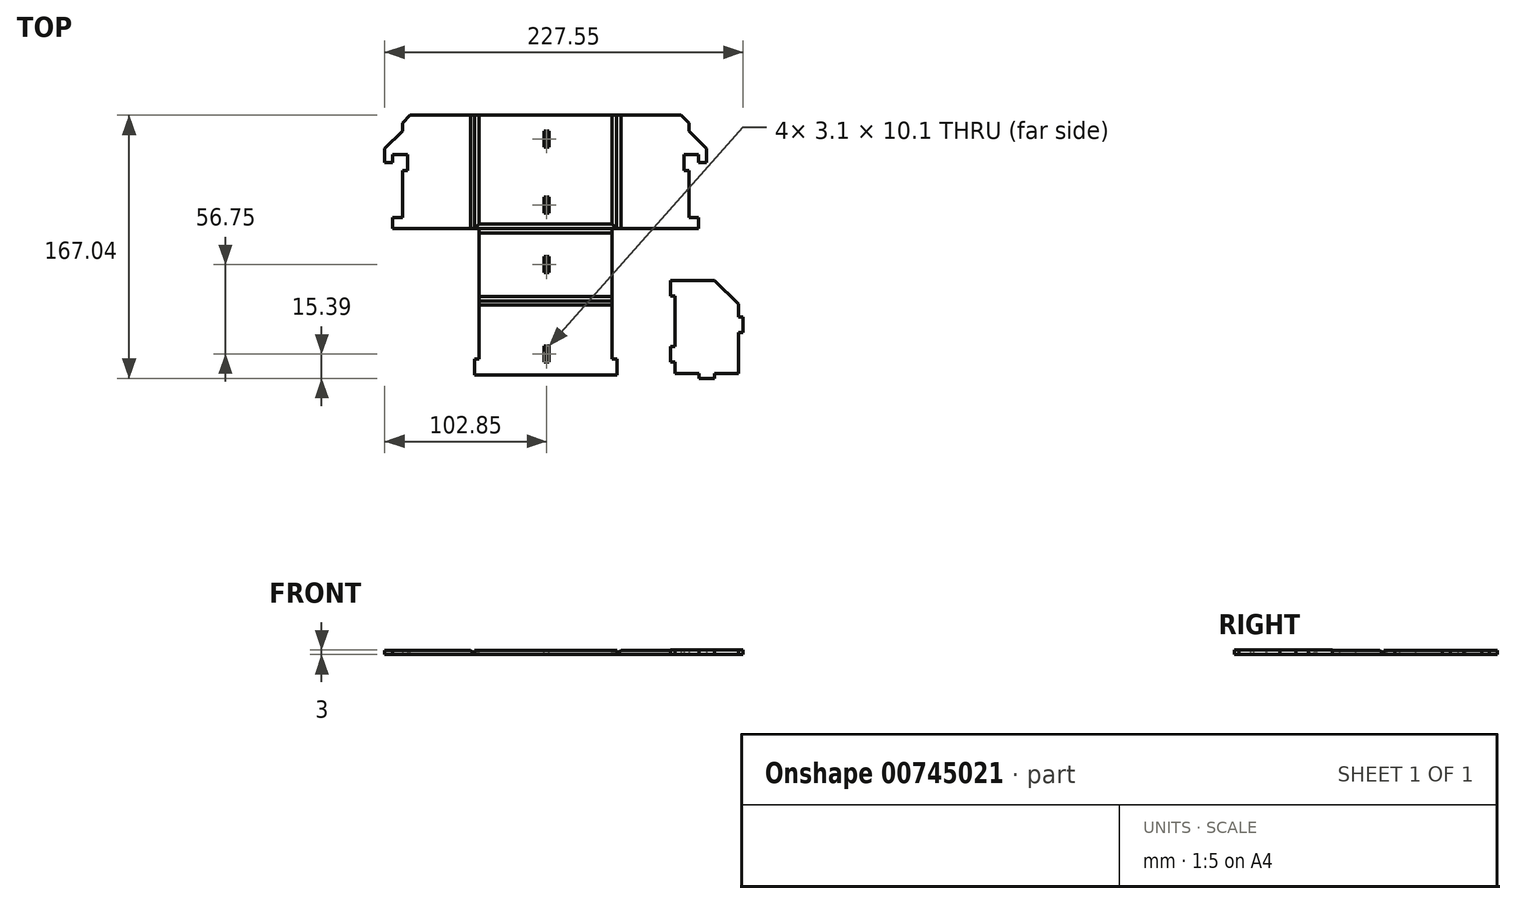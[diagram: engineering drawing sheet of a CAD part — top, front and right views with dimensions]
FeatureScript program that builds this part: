
annotation { "Feature Type Name" : "Feature", "Feature Type Description" : "" }
export const myFeature = defineFeature(function(context is Context, id is Id, definition is map)
    precondition{}
    {
        {
            var Q0;
            Q0=qCreatedBy(makeId("Top.planeOp"),FACE);
            var sketch = newSketch(context, id + "F0", { "sketchPlane" : qUnion([Q0])});
            skLineSegment(sketch, "E0.bottom", {"start": v(45, -36) * mm, "end": v(-45, -36) * mm});
            skLineSegment(sketch, "E0.top", {"start": v(45, 36) * mm, "end": v(-45, 36) * mm});
            skLineSegment(sketch, "E0.left", {"start": v(45, -36) * mm, "end": v(45, 36) * mm});
            skLineSegment(sketch, "E0.right", {"start": v(-45, -36) * mm, "end": v(-45, 36) * mm});
            skPoint(sketch, "E0.middle", {"position": v(0, 0) * mm});
            skLineSegment(sketch, "E1.bottom", {"start": v(45, 36) * mm, "end": v(91, 36) * mm});
            skLineSegment(sketch, "E1.top", {"start": v(45, -36) * mm, "end": v(91, -36) * mm});
            skLineSegment(sketch, "E1.left", {"start": v(45, 36) * mm, "end": v(45, -36) * mm});
            skLineSegment(sketch, "E1.right", {"start": v(91, 1) * mm, "end": v(91, -29) * mm});
            skLineSegment(sketch, "E2.bottom", {"start": v(-45, 36) * mm, "end": v(-91, 36) * mm});
            skLineSegment(sketch, "E2.top", {"start": v(-45, -36) * mm, "end": v(-91, -36) * mm});
            skLineSegment(sketch, "E2.left", {"start": v(-45, 36) * mm, "end": v(-45, -36) * mm});
            skLineSegment(sketch, "E2.right", {"start": v(-91, 36) * mm, "end": v(-91, 26) * mm});
            skLineSegment(sketch, "E3", {"start": v(91, 11) * mm, "end": v(97.2, 11) * mm});
            skLineSegment(sketch, "E4", {"start": v(97.2, 11) * mm, "end": v(97.2, 6) * mm});
            skLineSegment(sketch, "E5", {"start": v(97.2, 6) * mm, "end": v(102.2, 6) * mm});
            skPoint(sketch, "E6", {"position": v(102.2, 6) * mm});
            skLineSegment(sketch, "E7.bottom", {"start": v(91, -36) * mm, "end": v(97.2, -36) * mm});
            skLineSegment(sketch, "E7.top", {"start": v(91, -29) * mm, "end": v(97.2, -29) * mm});
            skLineSegment(sketch, "E7.right", {"start": v(97.2, -36) * mm, "end": v(97.2, -29) * mm});
            skLineSegment(sketch, "E8", {"start": v(91, 36) * mm, "end": v(91, 26) * mm});
            skLineSegment(sketch, "E9", {"start": v(91, 26) * mm, "end": v(102.2, 14.8) * mm});
            skLineSegment(sketch, "E10", {"start": v(102.2, 6) * mm, "end": v(102.2, 14.8) * mm});
            skLineSegment(sketch, "E11.MirrorCS", {"start": v(-91, 26) * mm, "end": v(-102.2, 14.8) * mm});
            skLineSegment(sketch, "E12.MirrorCS", {"start": v(-102.2, 6) * mm, "end": v(-102.2, 14.8) * mm});
            skLineSegment(sketch, "E13.MirrorCS", {"start": v(-97.2, 6) * mm, "end": v(-102.2, 6) * mm});
            skLineSegment(sketch, "E14.MirrorCS", {"start": v(-97.2, 11) * mm, "end": v(-97.2, 6) * mm});
            skLineSegment(sketch, "E15.MirrorCS", {"start": v(-91, 11) * mm, "end": v(-97.2, 11) * mm});
            skLineSegment(sketch, "E16.MirrorCS", {"start": v(-91, -29) * mm, "end": v(-97.2, -29) * mm});
            skLineSegment(sketch, "E17.MirrorCS", {"start": v(-97.2, -36) * mm, "end": v(-97.2, -29) * mm});
            skLineSegment(sketch, "E18.MirrorCS", {"start": v(-91, -36) * mm, "end": v(-97.2, -36) * mm});
            skLineSegment(sketch, "E19.trimOffspring", {"start": v(-91, 1) * mm, "end": v(-91, -29) * mm});
            skLineSegment(sketch, "E20.bottom", {"start": v(-42.2, -36) * mm, "end": v(42.2, -36) * mm});
            skLineSegment(sketch, "E20.top", {"start": v(-42.2, -81.8) * mm, "end": v(42.2, -81.8) * mm});
            skLineSegment(sketch, "E20.left", {"start": v(-42.2, -36) * mm, "end": v(-42.2, -81.8) * mm});
            skLineSegment(sketch, "E20.right", {"start": v(42.2, -36) * mm, "end": v(42.2, -81.8) * mm});
            skLineSegment(sketch, "E21.top", {"start": v(-42.2, -128.8) * mm, "end": v(42.2, -128.8) * mm});
            skLineSegment(sketch, "E21.left", {"start": v(-42.2, -81.8) * mm, "end": v(-42.2, -128.8) * mm});
            skLineSegment(sketch, "E21.right", {"start": v(42.2, -81.8) * mm, "end": v(42.2, -128.8) * mm});
            skLineSegment(sketch, "E22", {"start": v(91, 11) * mm, "end": v(87.8, 11) * mm});
            skLineSegment(sketch, "E23", {"start": v(87.8, 11) * mm, "end": v(87.8, 1) * mm});
            skLineSegment(sketch, "E24", {"start": v(87.8, 1) * mm, "end": v(91, 1) * mm});
            skLineSegment(sketch, "E25.MirrorCS", {"start": v(-91, 11) * mm, "end": v(-87.8, 11) * mm});
            skLineSegment(sketch, "E26.MirrorCS", {"start": v(-87.8, 11) * mm, "end": v(-87.8, 1) * mm});
            skLineSegment(sketch, "E27.MirrorCS", {"start": v(-87.8, 1) * mm, "end": v(-91, 1) * mm});
            skSolve(sketch);
        }
        {
            var Q0;
            Q0=makeQuery(id+"F0.imprint","IMPRINT",FACE,{"disambiguationData":[TD([[makeQuery(id+"F0.imprint","IMPRINT",EDGE,{"derivedFrom":sQuery(id+"F0.wireOp",EDGE,"E0.right")}),1.0]])]});
            var Q1;
            Q1=makeQuery(id+"F0.imprint","IMPRINT",FACE,{"disambiguationData":[TD([[makeQuery(id+"F0.imprint","IMPRINT",EDGE,{"derivedFrom":sQuery(id+"F0.wireOp",EDGE,"E0.left")}),-1.0]])]});
            extrude(context, id + "F1", {"entities" : qUnion([Q0, Q1]), "depth" : 2.8 * mm, "offsetDistance" : 25 * mm});
        }
        {
            var Q0;
            Q0=makeQuery(id+"F1.opExtrude","CAP_EDGE",EDGE,{"disambiguationData":[OSD([sQuery(id+"F0.wireOp",EDGE,"E0.left")])],"isStart":false});
            var Q1;
            Q1=makeQuery(id+"F1.opExtrude","CAP_EDGE",EDGE,{"disambiguationData":[OSD([sQuery(id+"F0.wireOp",EDGE,"E0.right")])],"isStart":false});
            chamfer(context, id + "F2", {"entities" : qUnion([Q0, Q1]), "width" : 2.8 * mm, "tangentPropagation" : true});
        }
        {
            var Q0;
            Q0=makeQuery(id+"F0.imprint","IMPRINT",FACE,{"disambiguationData":[TD([[makeQuery(id+"F0.imprint","IMPRINT",EDGE,{"derivedFrom":sQuery(id+"F0.wireOp",EDGE,"E0.top")}),1.0]])]});
            extrude(context, id + "F3", {"entities" : qUnion([Q0]), "depth" : 2.8 * mm, "offsetDistance" : 25 * mm});
        }
        {
            var Q0;
            Q0=makeQuery(id+"F3.opExtrude","CAP_EDGE",EDGE,{"disambiguationData":[OSD([sQuery(id+"F0.wireOp",EDGE,"E0.left")])],"isStart":false});
            var Q1;
            Q1=makeQuery(id+"F3.opExtrude","CAP_EDGE",EDGE,{"disambiguationData":[OSD([sQuery(id+"F0.wireOp",EDGE,"E0.right")])],"isStart":false});
            var Q2;
            Q2=makeQuery(id+"F3.opExtrude","CAP_EDGE",EDGE,{"disambiguationData":[OSD([sQuery(id+"F0.wireOp",EDGE,"E0.bottom")])],"isStart":false});
            chamfer(context, id + "F4", {"entities" : qUnion([Q0, Q1, Q2]), "width" : 2.8 * mm, "tangentPropagation" : true});
        }
        {
            var Q0;
            Q0=makeQuery(id+"F3.opExtrude","CAP_FACE",FACE,{"disambiguationData":[OSD([sQuery(id+"F0.wireOp",EDGE,"E0.bottom"),sQuery(id+"F0.wireOp",EDGE,"E0.top"),sQuery(id+"F0.wireOp",EDGE,"E0.left"),sQuery(id+"F0.wireOp",EDGE,"E0.right")])],"isStart":false});
            var sketch = newSketch(context, id + "F5", { "sketchPlane" : qUnion([Q0])});
            skLineSegment(sketch, "E28.bottom", {"start": v(-0.9, 26) * mm, "end": v(2.2, 26) * mm});
            skLineSegment(sketch, "E28.top", {"start": v(-0.9, 15.9) * mm, "end": v(2.2, 15.9) * mm});
            skLineSegment(sketch, "E28.left", {"start": v(-0.9, 26) * mm, "end": v(-0.9, 15.9) * mm});
            skLineSegment(sketch, "E28.right", {"start": v(2.2, 26) * mm, "end": v(2.2, 15.9) * mm});
            skLineSegment(sketch, "E29.bottom", {"start": v(-0.9, -15.9) * mm, "end": v(2.2, -15.9) * mm});
            skLineSegment(sketch, "E29.top", {"start": v(-0.9, -26) * mm, "end": v(2.2, -26) * mm});
            skLineSegment(sketch, "E29.left", {"start": v(-0.9, -15.9) * mm, "end": v(-0.9, -26) * mm});
            skLineSegment(sketch, "E29.right", {"start": v(2.2, -15.9) * mm, "end": v(2.2, -26) * mm});
            skSolve(sketch);
        }
        {
            var Q0;
            Q0=makeQuery(id+"F5.imprint","IMPRINT",FACE,{"disambiguationData":[TD([[makeQuery(id+"F5.imprint","IMPRINT",EDGE,{"derivedFrom":sQuery(id+"F5.wireOp",EDGE,"E28.bottom")}),-1.0]])]});
            var Q1;
            Q1=makeQuery(id+"F5.imprint","IMPRINT",FACE,{"disambiguationData":[TD([[makeQuery(id+"F5.imprint","IMPRINT",EDGE,{"derivedFrom":sQuery(id+"F5.wireOp",EDGE,"E29.bottom")}),-1.0]])]});
            extrude(context, id + "F6", {"entities" : qUnion([Q0, Q1]), "operationType" : NewBodyOperationType.REMOVE, "oppositeDirection" : true, "depth" : 3 * mm, "offsetDistance" : 25 * mm});
        }
        {
            var Q0;
            Q0=makeQuery(id+"F0.imprint","IMPRINT",FACE,{"disambiguationData":[TD([[makeQuery(id+"F0.imprint","IMPRINT",EDGE,{"derivedFrom":sQuery(id+"F0.wireOp",EDGE,"E20.top")}),1.0]])]});
            extrude(context, id + "F7", {"entities" : qUnion([Q0]), "depth" : 2.8 * mm, "offsetDistance" : 25 * mm});
        }
        {
            var Q0;
            Q0=makeQuery(id+"F7.opExtrude","CAP_EDGE",EDGE,{"disambiguationData":[OSD([sQuery(id+"F0.wireOp",EDGE,"E0.bottom")])],"isStart":false});
            var Q1;
            Q1=makeQuery(id+"F7.opExtrude","CAP_EDGE",EDGE,{"disambiguationData":[OSD([sQuery(id+"F0.wireOp",EDGE,"E20.top")])],"isStart":false});
            chamfer(context, id + "F8", {"entities" : qUnion([Q0, Q1]), "width" : 2.8 * mm, "tangentPropagation" : true});
        }
        {
            var Q0;
            Q0=makeQuery(id+"F0.imprint","IMPRINT",FACE,{"disambiguationData":[TD([[makeQuery(id+"F0.imprint","IMPRINT",EDGE,{"derivedFrom":sQuery(id+"F0.wireOp",EDGE,"E20.top")}),-1.0]])]});
            extrude(context, id + "F9", {"entities" : qUnion([Q0]), "depth" : 2.8 * mm, "offsetDistance" : 25 * mm});
        }
        {
            var Q0;
            Q0=makeQuery(id+"F9.opExtrude","CAP_EDGE",EDGE,{"disambiguationData":[OSD([sQuery(id+"F0.wireOp",EDGE,"E20.top")])],"isStart":false});
            chamfer(context, id + "F10", {"entities" : qUnion([Q0]), "width" : 2.8 * mm, "tangentPropagation" : true});
        }
        {
            var Q0;
            Q0=makeQuery(id+"F9.opExtrude","SWEPT_FACE",FACE,{"disambiguationData":[OSD([sQuery(id+"F0.wireOp",EDGE,"E21.left")])]});
            var sketch = newSketch(context, id + "F11", { "sketchPlane" : qUnion([Q0])});
            skLineSegment(sketch, "E30.bottom", {"start": v(128.8, 0) * mm, "end": v(118.8, 0) * mm});
            skLineSegment(sketch, "E30.top", {"start": v(128.8, 2.8) * mm, "end": v(118.8, 2.8) * mm});
            skLineSegment(sketch, "E30.left", {"start": v(128.8, 0) * mm, "end": v(128.8, 2.8) * mm});
            skLineSegment(sketch, "E30.right", {"start": v(118.8, 0) * mm, "end": v(118.8, 2.8) * mm});
            skSolve(sketch);
        }
        {
            var Q0;
            Q0=makeQuery(id+"F11.imprint","IMPRINT",FACE,{"disambiguationData":[TD([[makeQuery(id+"F11.imprint","IMPRINT",EDGE,{"derivedFrom":sQuery(id+"F11.wireOp",EDGE,"E30.bottom")}),1.0]])]});
            var Q1;
            {var subQ2=sQuery(id+"F11.wireOp",EDGE,"E30.left");Q1=makeQuery(id+"F11.imprint","IMPRINT",FACE,{"disambiguationData":[TD([[makeQuery(id+"F11.imprint","IMPRINT",EDGE,{"derivedFrom":subQ2}),1.0]])]});}
            extrude(context, id + "F12", {"entities" : qUnion([Q0, Q1]), "depth" : 3 * mm, "offsetDistance" : 25 * mm});
        }
        {
            var Q0;
            Q0=makeQuery(id+"F12.opExtrude","SWEPT_BODY",BODY,{"disambiguationData":[OSD([sQuery(id+"F11.wireOp",EDGE,"E30.bottom"),sQuery(id+"F11.wireOp",EDGE,"E30.top"),sQuery(id+"F11.wireOp",EDGE,"E30.left"),sQuery(id+"F11.wireOp",EDGE,"E30.right")])]});
            var Q1;
            Q1=qCreatedBy(makeId("Right.planeOp"),FACE);
            mirror(context, id + "F13", {"operationType" : NewBodyOperationType.ADD, "entities" : qUnion([Q0]), "mirrorPlane" : qUnion([Q1])});
        }
        {
            var Q0;
            Q0=makeQuery(id+"F7.opExtrude","CAP_FACE",FACE,{"disambiguationData":[OSD([sQuery(id+"F0.wireOp",EDGE,"E0.bottom"),sQuery(id+"F0.wireOp",EDGE,"E20.top"),sQuery(id+"F0.wireOp",EDGE,"E20.left"),sQuery(id+"F0.wireOp",EDGE,"E20.right")])],"isStart":false});
            var sketch = newSketch(context, id + "F14", { "sketchPlane" : qUnion([Q0])});
            skLineSegment(sketch, "E31.bottom", {"start": v(-0.9, -53.85) * mm, "end": v(2.2, -53.85) * mm});
            skLineSegment(sketch, "E31.top", {"start": v(-0.9, -63.95) * mm, "end": v(2.2, -63.95) * mm});
            skLineSegment(sketch, "E31.left", {"start": v(-0.9, -53.85) * mm, "end": v(-0.9, -63.95) * mm});
            skLineSegment(sketch, "E31.right", {"start": v(2.2, -53.85) * mm, "end": v(2.2, -63.95) * mm});
            skSolve(sketch);
        }
        {
            var Q0;
            {var subQ0=makeQuery(id+"F12.opExtrude","SWEPT_FACE",FACE,{"disambiguationData":[OSD([sQuery(id+"F11.wireOp",EDGE,"E30.top")])]});Q0=makeQuery(id+"F13.boolean.opBoolean","MERGE",FACE,{"derivedFrom":[makeQuery(id+"F9.opExtrude","CAP_FACE",FACE,{"disambiguationData":[OSD([sQuery(id+"F0.wireOp",EDGE,"E20.top"),sQuery(id+"F0.wireOp",EDGE,"E21.top"),sQuery(id+"F0.wireOp",EDGE,"E21.left"),sQuery(id+"F0.wireOp",EDGE,"E21.right")])],"isStart":false}),subQ0,makeQuery(id+"F13.opPattern","COPY",FACE,{"derivedFrom":subQ0,"instanceName":"1"})]});}
            var sketch = newSketch(context, id + "F15", { "sketchPlane" : qUnion([Q0])});
            skLineSegment(sketch, "E32.bottom", {"start": v(-0.9, -110.6) * mm, "end": v(2.2, -110.6) * mm});
            skLineSegment(sketch, "E32.top", {"start": v(-0.9, -120.7) * mm, "end": v(2.2, -120.7) * mm});
            skLineSegment(sketch, "E32.left", {"start": v(-0.9, -110.6) * mm, "end": v(-0.9, -120.7) * mm});
            skLineSegment(sketch, "E32.right", {"start": v(2.2, -110.6) * mm, "end": v(2.2, -120.7) * mm});
            skSolve(sketch);
        }
        {
            var Q0;
            Q0=makeQuery(id+"F15.imprint","IMPRINT",FACE,{"disambiguationData":[TD([[makeQuery(id+"F15.imprint","IMPRINT",EDGE,{"derivedFrom":sQuery(id+"F15.wireOp",EDGE,"E32.bottom")}),-1.0]])]});
            var Q1;
            Q1=makeQuery(id+"F14.imprint","IMPRINT",FACE,{"disambiguationData":[TD([[makeQuery(id+"F14.imprint","IMPRINT",EDGE,{"derivedFrom":sQuery(id+"F14.wireOp",EDGE,"E31.bottom")}),-1.0]])]});
            extrude(context, id + "F16", {"entities" : qUnion([Q0, Q1]), "operationType" : NewBodyOperationType.REMOVE, "oppositeDirection" : true, "depth" : 4 * mm, "offsetDistance" : 25 * mm});
        }
        {
            var Q0;
            Q0=qCreatedBy(makeId("Top.planeOp"),FACE);
            var sketch = newSketch(context, id + "F17", { "sketchPlane" : qUnion([Q0])});
            skLineSegment(sketch, "E33.bottom", {"start": v(82.15, -58.84) * mm, "end": v(122.35, -58.84) * mm});
            skLineSegment(sketch, "E33.top", {"start": v(82.15, -128.04) * mm, "end": v(97.25, -128.04) * mm});
            skLineSegment(sketch, "E33.left", {"start": v(82.15, -58.84) * mm, "end": v(82.15, -68.89) * mm});
            skLineSegment(sketch, "E33.right", {"start": v(122.35, -58.84) * mm, "end": v(122.35, -91.99) * mm});
            skPoint(sketch, "E34", {"position": v(82.15, -68.89) * mm});
            skLineSegment(sketch, "E35", {"start": v(82.15, -68.89) * mm, "end": v(79.15, -68.89) * mm});
            skLineSegment(sketch, "E36", {"start": v(79.15, -68.89) * mm, "end": v(79.15, -78.89) * mm});
            skLineSegment(sketch, "E37", {"start": v(79.15, -78.89) * mm, "end": v(82.15, -78.89) * mm});
            skLineSegment(sketch, "E38.trimOffspring", {"start": v(82.15, -78.89) * mm, "end": v(82.15, -110.79) * mm});
            skLineSegment(sketch, "E39", {"start": v(102.25, -131.04) * mm, "end": v(97.25, -131.04) * mm});
            skLineSegment(sketch, "E40", {"start": v(97.25, -131.04) * mm, "end": v(97.25, -128.04) * mm});
            skLineSegment(sketch, "E41", {"start": v(102.25, -131.04) * mm, "end": v(107.25, -131.04) * mm});
            skLineSegment(sketch, "E42", {"start": v(107.25, -131.04) * mm, "end": v(107.25, -128.04) * mm});
            skLineSegment(sketch, "E43.trimOffspring", {"start": v(107.25, -128.04) * mm, "end": v(122.35, -128.04) * mm});
            skLineSegment(sketch, "E44", {"start": v(82.15, -68.89) * mm, "end": v(122.35, -68.89) * mm});
            skPoint(sketch, "E45", {"position": v(122.35, -101.99) * mm});
            skLineSegment(sketch, "E46", {"start": v(122.35, -101.99) * mm, "end": v(125.35, -101.99) * mm});
            skLineSegment(sketch, "E47", {"start": v(125.35, -101.99) * mm, "end": v(125.35, -91.99) * mm});
            skLineSegment(sketch, "E48", {"start": v(125.35, -91.99) * mm, "end": v(122.35, -91.99) * mm});
            skLineSegment(sketch, "E49.trimOffspring", {"start": v(122.35, -101.99) * mm, "end": v(122.35, -128.04) * mm});
            skPoint(sketch, "E50", {"position": v(82.15, -110.79) * mm});
            skLineSegment(sketch, "E51", {"start": v(82.15, -110.79) * mm, "end": v(79.15, -110.79) * mm});
            skLineSegment(sketch, "E52", {"start": v(79.15, -110.79) * mm, "end": v(79.15, -120.79) * mm});
            skLineSegment(sketch, "E53", {"start": v(79.15, -120.79) * mm, "end": v(82.15, -120.79) * mm});
            skLineSegment(sketch, "E54.trimOffspring", {"start": v(82.15, -120.79) * mm, "end": v(82.15, -128.04) * mm});
            skSolve(sketch);
        }
        {
            var Q0;
            Q0=makeQuery(id+"F17.imprint","IMPRINT",FACE,{"disambiguationData":[TD([[makeQuery(id+"F17.imprint","IMPRINT",EDGE,{"derivedFrom":sQuery(id+"F17.wireOp",EDGE,"E33.top")}),1.0]])]});
            extrude(context, id + "F18", {"entities" : qUnion([Q0]), "depth" : 3 * mm, "offsetDistance" : 25 * mm});
        }
        {
            var Q0;
            Q0=makeQuery(id+"F1.opExtrude","SWEPT_EDGE",EDGE,{"disambiguationData":[OSD([sQuery(id+"F0.wireOp",EDGE,"E1.bottom"),sQuery(id+"F0.wireOp",EDGE,"E8")])]});
            var Q1;
            Q1=makeQuery(id+"F1.opExtrude","SWEPT_EDGE",EDGE,{"disambiguationData":[OSD([sQuery(id+"F0.wireOp",EDGE,"E2.bottom"),sQuery(id+"F0.wireOp",EDGE,"E2.right")])]});
            chamfer(context, id + "F19", {"entities" : qUnion([Q0, Q1]), "width" : 5 * mm, "tangentPropagation" : true});
        }
        {
            var Q0;
            Q0=makeQuery(id+"F18.opExtrude","SWEPT_EDGE",EDGE,{"disambiguationData":[OSD([sQuery(id+"F17.wireOp",EDGE,"E33.right"),sQuery(id+"F17.wireOp",EDGE,"E44")])]});
            chamfer(context, id + "F20", {"entities" : qUnion([Q0]), "width" : 15 * mm, "tangentPropagation" : true});
        }
    });
